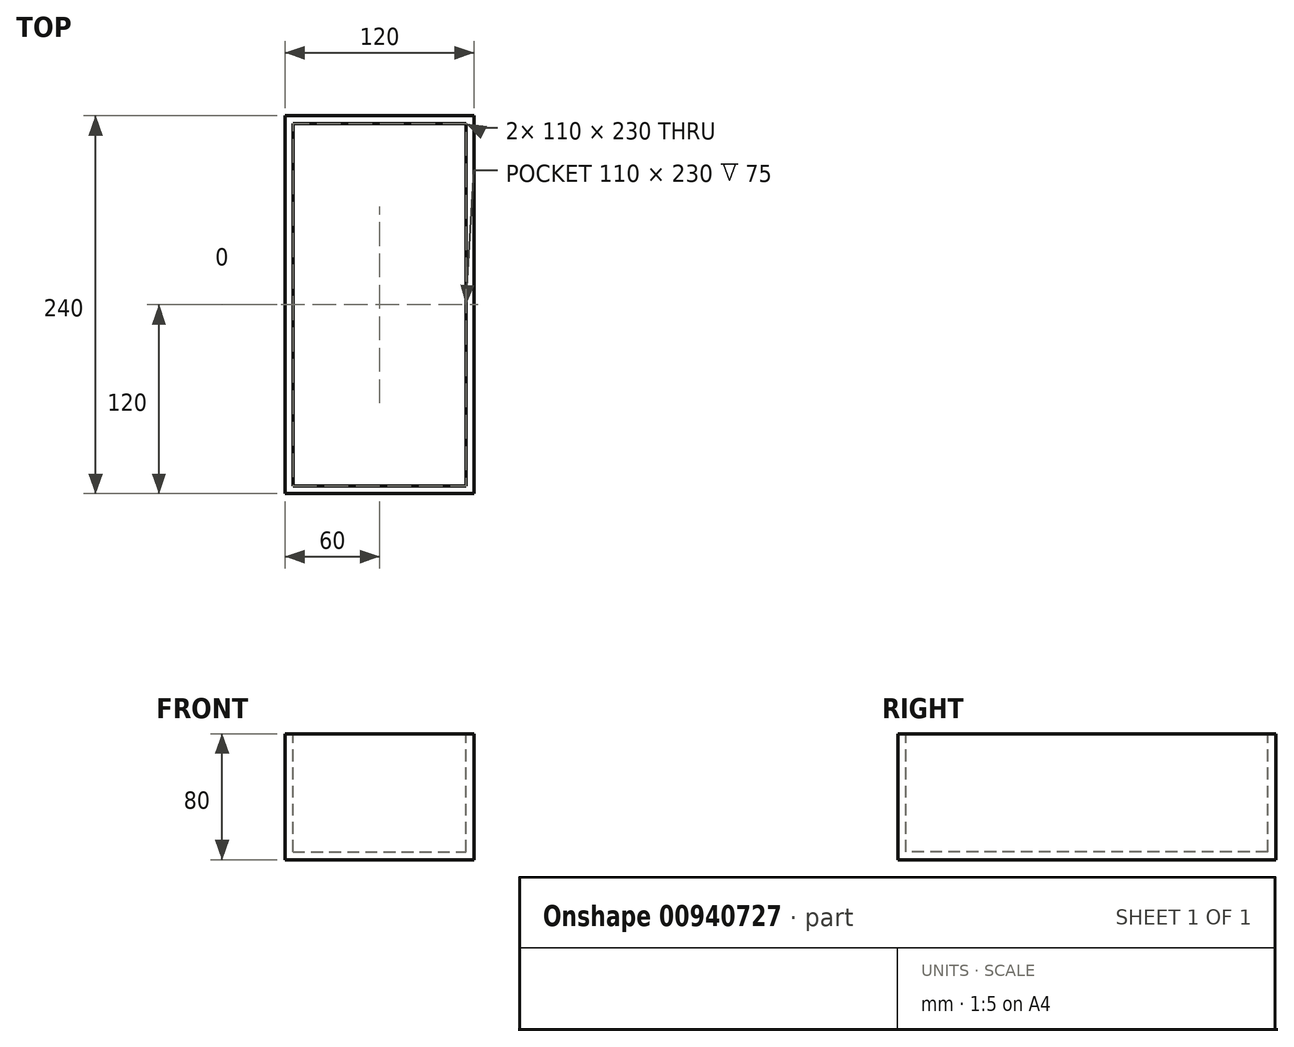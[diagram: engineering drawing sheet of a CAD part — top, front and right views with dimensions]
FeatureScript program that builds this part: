
annotation { "Feature Type Name" : "Feature", "Feature Type Description" : "" }
export const myFeature = defineFeature(function(context is Context, id is Id, definition is map)
    precondition{}
    {
        {
            var Q0;
            Q0=qCreatedBy(makeId("Top.planeOp"),FACE);
            var sketch = newSketch(context, id + "F0", { "sketchPlane" : qUnion([Q0])});
            skLineSegment(sketch, "E0.bottom", {"start": v(0, 0) * mm, "end": v(120, 0) * mm});
            skLineSegment(sketch, "E0.top", {"start": v(0, 240) * mm, "end": v(120, 240) * mm});
            skLineSegment(sketch, "E0.left", {"start": v(0, 0) * mm, "end": v(0, 240) * mm});
            skLineSegment(sketch, "E0.right", {"start": v(120, 0) * mm, "end": v(120, 240) * mm});
            skSolve(sketch);
        }
        {
            var Q0;
            Q0 = qSketchRegion(id + "F0", true);
            extrude(context, id + "F1", {"entities" : qUnion([Q0]), "depth" : 80 * mm, "offsetDistance" : 25 * mm});
        }
        {
            var Q0;
            Q0=makeQuery(id+"F1.opExtrude","CAP_FACE",FACE,{"disambiguationData":[OSD([sQuery(id+"F0.wireOp",EDGE,"E0.bottom"),sQuery(id+"F0.wireOp",EDGE,"E0.top"),sQuery(id+"F0.wireOp",EDGE,"E0.left"),sQuery(id+"F0.wireOp",EDGE,"E0.right")])],"isStart":false});
            var sketch = newSketch(context, id + "F2", { "sketchPlane" : qUnion([Q0])});
            skLineSegment(sketch, "E1.bottom", {"start": v(5, 235) * mm, "end": v(115, 235) * mm});
            skLineSegment(sketch, "E1.top", {"start": v(5, 5) * mm, "end": v(115, 5) * mm});
            skLineSegment(sketch, "E1.left", {"start": v(5, 235) * mm, "end": v(5, 5) * mm});
            skLineSegment(sketch, "E1.right", {"start": v(115, 235) * mm, "end": v(115, 5) * mm});
            skLineSegment(sketch, "E2", {"start": v(0, 152.28) * mm, "end": v(5, 152.28) * mm});
            skLineSegment(sketch, "E3", {"start": v(60, 0) * mm, "end": v(60, 5) * mm});
            skSolve(sketch);
        }
        {
            var Q0;
            {var subQ1=sQuery(id+"F2.wireOp",EDGE,"E1.bottom");Q0=makeQuery(id+"F2.imprint","IMPRINT",FACE,{"disambiguationData":[TD([[makeQuery(id+"F2.imprint","IMPRINT",EDGE,{"derivedFrom":subQ1}),-1.0]])]});}
            extrude(context, id + "F3", {"entities" : qUnion([Q0]), "operationType" : NewBodyOperationType.REMOVE, "oppositeDirection" : true, "depth" : 75 * mm, "offsetDistance" : 25 * mm});
        }
    });
